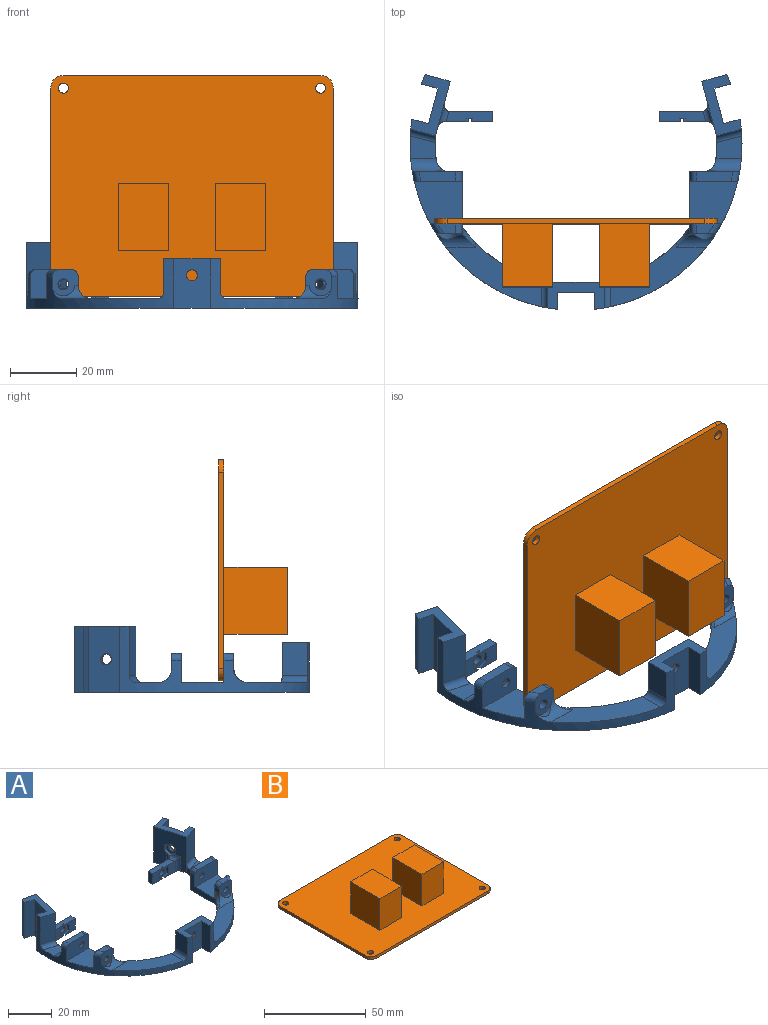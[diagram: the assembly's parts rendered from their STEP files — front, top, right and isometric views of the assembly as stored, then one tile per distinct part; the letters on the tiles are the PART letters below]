
ASSEMBLY  parts=2 mates=1
PART A: 148 faces, bbox 100.8x70.8x20.2 mm
  f0: plane 17x15mm, normal (0,1,0), area 226.7mm2, adj f1,f2,f28,f39,f41,f95,f96,f97
  f1: plane 10x7.77mm, normal (-1,0,0), area 77.7mm2, adj f0,f3,f127,f147
  f2: plane 10x7.77mm, normal (1,0,0), area 77.7mm2, adj f0,f4,f129,f147
  f3: cylinder r=50mm len=57.25mm, axis (0,0,-1), area 383.3mm2, adj f1,f5,f10,f27,f28,f29,f30,f35
  f4: cylinder r=50mm len=57.25mm, axis (0,0,-1), area 383.3mm2, adj f2,f7,f11,f23,f24,f28,f42,f43
  f5: plane 15x5.2mm, normal (1,0,0), area 77.9mm2, adj f3,f6,f28,f147
  f6: plane 15x11mm, normal (0,-1,0), area 156.4mm2, adj f5,f7,f22,f28,f147
  f7: plane 15x5.2mm, normal (-1,0,0), area 77.9mm2, adj f4,f6,f28,f147
  f8: cylinder r=1.65mm len=3.3mm, axis (0,1,0), area 31.1mm2, adj f43,f58
  f9: cylinder r=1.65mm len=3.3mm, axis (0,1,0), area 31.1mm2, adj f38,f60
  f10: cylinder r=4mm len=11.73mm, axis (1,0,0), area 33mm2, adj f3,f40,f60,f77,f146
  f11: cylinder r=4mm len=11.73mm, axis (1,0,0), area 33mm2, adj f4,f42,f43,f78,f145
  f12: plane 6.48x6mm, normal (0,-1,0), area 28mm2, adj f13,f28,f116,f132,f133,f134
  f13: plane 14.07x3.07mm, normal (0,0,1), area 40mm2, adj f12,f116,f117,f118,f124,f125,f134,f135
  f14: plane 7.09x6.07mm, normal (0,-1,0), area 31.7mm2, adj f16,f28,f122,f123,f138,f139,f140
  f15: plane 6.48x6mm, normal (0,-1,0), area 28mm2, adj f16,f28,f120,f141,f142,f143
  f16: plane 14.07x3.07mm, normal (0,0,1), area 40mm2, adj f14,f15,f119,f120,f121,f122,f140,f141
  f17: cylinder r=1.65mm len=3.3mm, axis (0,-1,0), area 20.7mm2, adj f119,f144
  f18: cylinder r=1.65mm len=3.3mm, axis (0,-1,0), area 20.7mm2, adj f117,f137
  f19: plane 20x16.42mm, normal (0.97,-0.26,0), area 256.5mm2, adj f26,f28,f29,f31,f35,f102,f103,f104
  f20: cylinder r=1.65mm len=3.58mm, axis (-0.97,-0.26,0), area 15.6mm2, adj f55,f115
  f21: cylinder r=1.65mm len=3.58mm, axis (0.97,-0.26,0), area 15.6mm2, adj f34,f108
  f22: cylinder r=1.65mm len=3.3mm, axis (0,1,0), area 15.6mm2, adj f6,f101
  f23: plane 15.18x11.9mm, normal (0,1,0), area 76.2mm2, adj f4,f24,f25,f28,f44,f57,f73,f74
  f24: cylinder r=4mm len=9.58mm, axis (-1,0,0), area 51.2mm2, adj f4,f23,f25,f47,f48,f88,f93
  f25: cylinder r=4mm len=4.88mm, axis (0,0,-1), area 23.2mm2, adj f23,f24,f28,f47,f88,f89
  f26: cylinder r=42.36mm len=7.17mm, axis (0,0,-1), area 22.4mm2, adj f19,f27,f28,f79,f80,f130
  f27: plane 7.85x6.71mm, normal (0,0,1), area 43.6mm2, adj f3,f26,f79,f130
  f28: plane 100x70.66mm, normal (0,0,-1), area 1521.3mm2, adj f0,f3,f4,f5,f6,f7,f12,f14
  f29: plane 15x7.51mm, normal (-0.26,-0.97,0), area 116.6mm2, adj f3,f19,f35,f130
  f30: plane 20x5.02mm, normal (0.26,0.97,0), area 103.9mm2, adj f3,f28,f34,f35
  f31: plane 20x7.51mm, normal (0.26,0.97,0), area 155.4mm2, adj f19,f28,f32,f35
  f32: cylinder r=50mm len=20mm, axis (0,0,-1), area 60.6mm2, adj f28,f31,f33,f35
  f33: plane 20x5.02mm, normal (-0.26,-0.97,0), area 103.9mm2, adj f28,f32,f34,f35
  f34: plane 20x10.63mm, normal (-0.97,0.26,0), area 211.4mm2, adj f21,f28,f30,f33,f35
  f35: plane 18.43x11.91mm, normal (0,0,1), area 81mm2, adj f3,f19,f29,f30,f31,f32,f33,f34
  f36: plane 18.8x9.76mm, normal (1,0,0), area 77.4mm2, adj f28,f37,f38,f60,f62,f63,f68,f69
  f37: plane 14.44x12.8mm, normal (0,0,1), area 158mm2, adj f3,f36,f38,f62
  f38: plane 9.57x8.76mm, normal (0,1,0), area 73.4mm2, adj f3,f9,f36,f37,f61,f67,f68
  f39: cylinder r=42.36mm len=25.39mm, axis (0,0,-1), area 96.7mm2, adj f0,f28,f40,f75,f77,f127
  f40: plane 28.73x19.27mm, normal (0,0,1), area 214.2mm2, adj f3,f10,f39,f77,f127
  f41: cylinder r=42.36mm len=25.39mm, axis (0,0,-1), area 96.7mm2, adj f0,f28,f42,f76,f78,f129
  f42: plane 28.73x19.27mm, normal (0,0,1), area 214.2mm2, adj f4,f11,f41,f78,f129
  f43: plane 7.95x7.79mm, normal (0,-1,0), area 43.6mm2, adj f4,f8,f11,f44,f59,f71,f72,f145
  f44: plane 18.8x9.76mm, normal (-1,0,0), area 77.4mm2, adj f23,f28,f43,f45,f46,f58,f71,f73
  f45: plane 14.44x12.8mm, normal (0,0,1), area 158mm2, adj f4,f44,f46,f58
  f46: plane 14.44x8.76mm, normal (0,-1,0), area 116.1mm2, adj f4,f44,f45,f57,f66,f73,f74
  f47: cylinder r=42.36mm len=7.17mm, axis (0,0,-1), area 22.4mm2, adj f24,f25,f28,f48,f53,f128
  f48: plane 7.85x6.71mm, normal (0,0,1), area 43.6mm2, adj f4,f24,f47,f128
  f49: plane 15x7.51mm, normal (0.26,-0.97,0), area 116.6mm2, adj f4,f53,f56,f128
  f50: plane 20x5.02mm, normal (0.26,-0.97,0), area 103.9mm2, adj f28,f51,f55,f56
  f51: cylinder r=50mm len=20mm, axis (0,0,-1), area 60.6mm2, adj f28,f50,f52,f56
  f52: plane 20x7.51mm, normal (-0.26,0.97,0), area 155.4mm2, adj f28,f51,f53,f56
  f53: plane 20x16.42mm, normal (-0.97,-0.26,0), area 256.5mm2, adj f28,f47,f49,f52,f56,f109,f110,f111
  f54: plane 20x5.02mm, normal (-0.26,0.97,0), area 103.9mm2, adj f4,f28,f55,f56
  f55: plane 20x10.63mm, normal (0.97,0.26,0), area 211.4mm2, adj f20,f28,f50,f54,f56
  f56: plane 18.43x11.91mm, normal (0,0,1), area 81mm2, adj f4,f49,f50,f51,f52,f53,f54,f55
  f57: plane 11x3mm, normal (0,0,1), area 32.1mm2, adj f23,f46,f73,f74
  f58: plane 9.57x8.76mm, normal (0,1,0), area 73.4mm2, adj f4,f8,f44,f45,f59,f71,f72
  f59: plane 5.28x3mm, normal (0,0,1), area 13.1mm2, adj f43,f58,f71,f72
  f60: plane 7.95x7.79mm, normal (0,-1,0), area 43.6mm2, adj f3,f9,f10,f36,f61,f67,f68,f146
  f61: plane 5.28x3mm, normal (0,0,1), area 13.1mm2, adj f38,f60,f67,f68
  f62: plane 14.44x8.76mm, normal (0,-1,0), area 116.1mm2, adj f3,f36,f37,f64,f65,f69,f70
  f63: plane 15.18x11.9mm, normal (0,1,0), area 76.2mm2, adj f3,f28,f36,f64,f69,f70,f79,f80
  f64: plane 11x3mm, normal (0,0,1), area 32.1mm2, adj f62,f63,f69,f70
  f65: cylinder r=1.65mm len=3.3mm, axis (0,1,0), area 15.6mm2, adj f62,f87
  f66: cylinder r=1.65mm len=3.3mm, axis (0,1,0), area 15.6mm2, adj f46,f94
  f67: torus R=48mm, axis (0,0,1), area 11mm2, adj f3,f38,f60,f61
  f68: cylinder r=2mm len=3mm, axis (0,-1,0), area 9.4mm2, adj f36,f38,f60,f61
  f69: cylinder r=2mm len=3mm, axis (0,-1,0), area 9.4mm2, adj f36,f62,f63,f64
  f70: torus R=48mm, axis (0,0,1), area 9.5mm2, adj f3,f62,f63,f64
  f71: cylinder r=2mm len=3mm, axis (0,1,0), area 9.4mm2, adj f43,f44,f58,f59
  f72: torus R=48mm, axis (0,0,1), area 11mm2, adj f4,f43,f58,f59
  f73: cylinder r=2mm len=3mm, axis (0,1,0), area 9.4mm2, adj f23,f44,f46,f57
  f74: torus R=48mm, axis (0,0,1), area 9.5mm2, adj f4,f23,f46,f57
  f75: cylinder r=2mm len=7mm, axis (0,0,-1), area 7.9mm2, adj f28,f36,f39,f77
  f76: cylinder r=2mm len=7mm, axis (0,0,-1), area 7.9mm2, adj f28,f41,f44,f78
  f77: cylinder r=4mm len=6.78mm, axis (0,1,0), area 11.5mm2, adj f10,f36,f39,f40,f75
  f78: cylinder r=4mm len=6.78mm, axis (0,-1,0), area 11.5mm2, adj f11,f41,f42,f44,f76
  f79: cylinder r=4mm len=9.58mm, axis (-1,0,0), area 51.2mm2, adj f3,f26,f27,f63,f80,f84,f86
  f80: cylinder r=4mm len=4.88mm, axis (0,0,-1), area 23.2mm2, adj f26,f28,f63,f79,f85,f86
  f81: plane 2.86x1.65mm, normal (-0.5,0,-0.87), area 5mm2, adj f63,f82,f83,f87
  f82: plane 3.3x1.5mm, normal (-1,0,0), area 5mm2, adj f63,f81,f85,f87
  f83: plane 2.86x1.65mm, normal (0.5,0,-0.87), area 5mm2, adj f63,f81,f84,f87
  f84: plane 3.3x1.73mm, normal (1,0,0), area 5.1mm2, adj f63,f79,f83,f86,f87
  f85: plane 2.86x1.65mm, normal (-0.5,0,0.87), area 5mm2, adj f63,f80,f82,f86,f87
  f86: plane 2.89x2.14mm, normal (0.5,0,0.87), area 6mm2, adj f79,f80,f84,f85,f87
  f87: plane 6.6x5.72mm, normal (0,1,0), area 19.7mm2, adj f65,f81,f82,f83,f84,f85,f86
  f88: plane 2.89x2.14mm, normal (-0.5,0,0.87), area 6mm2, adj f24,f25,f89,f93,f94
  f89: plane 2.86x1.65mm, normal (0.5,0,0.87), area 5mm2, adj f23,f25,f88,f90,f94
  f90: plane 3.3x1.5mm, normal (1,0,0), area 5mm2, adj f23,f89,f91,f94
  f91: plane 2.86x1.65mm, normal (0.5,0,-0.87), area 5mm2, adj f23,f90,f92,f94
  f92: plane 2.86x1.65mm, normal (-0.5,0,-0.87), area 5mm2, adj f23,f91,f93,f94
  f93: plane 3.3x1.73mm, normal (-1,0,0), area 5.1mm2, adj f23,f24,f88,f92,f94
  f94: plane 6.6x5.72mm, normal (0,1,0), area 19.7mm2, adj f66,f88,f89,f90,f91,f92,f93
  f95: plane 2.86x1.65mm, normal (0.5,0,-0.87), area 5mm2, adj f0,f96,f100,f101
  f96: plane 2.86x1.65mm, normal (-0.5,0,-0.87), area 5mm2, adj f0,f95,f97,f101
  f97: plane 3.3x1.5mm, normal (-1,0,0), area 5mm2, adj f0,f96,f98,f101
  f98: plane 2.86x1.65mm, normal (-0.5,0,0.87), area 5mm2, adj f0,f97,f99,f101
  f99: plane 2.86x1.65mm, normal (0.5,0,0.87), area 5mm2, adj f0,f98,f100,f101
  f100: plane 3.3x1.5mm, normal (1,0,0), area 5mm2, adj f0,f95,f99,f101
  f101: plane 6.6x5.72mm, normal (0,1,0), area 19.7mm2, adj f22,f95,f96,f97,f98,f99,f100
  f102: plane 3.3x2.8mm, normal (0.13,0.48,0.87), area 5.3mm2, adj f19,f103,f107,f108,f125
  f103: plane 3.31x2.22mm, normal (-0.13,-0.48,0.87), area 5.3mm2, adj f19,f102,f104,f108,f124,f125
  f104: plane 3.3x1.45mm, normal (-0.26,-0.97,0), area 5mm2, adj f19,f103,f105,f108
  f105: plane 3.15x2.19mm, normal (-0.13,-0.48,-0.87), area 5mm2, adj f19,f104,f106,f108
  f106: plane 3.15x2.19mm, normal (0.13,0.48,-0.87), area 5mm2, adj f19,f105,f107,f108
  f107: plane 3.3x1.45mm, normal (0.26,0.97,0), area 4.9mm2, adj f19,f102,f106,f108
  f108: plane 6.6x5.52mm, normal (0.97,-0.26,0), area 19.7mm2, adj f21,f102,f103,f104,f105,f106,f107
  f109: plane 3.3x2.8mm, normal (-0.13,0.48,0.87), area 5.3mm2, adj f53,f110,f114,f115,f122
  f110: plane 3.3x1.45mm, normal (-0.26,0.97,0), area 4.9mm2, adj f53,f109,f111,f115
  f111: plane 3.15x2.19mm, normal (-0.13,0.48,-0.87), area 4.9mm2, adj f53,f110,f112,f115
  f112: plane 3.15x2.19mm, normal (0.13,-0.48,-0.87), area 5mm2, adj f53,f111,f113,f115
  f113: plane 3.3x1.45mm, normal (0.26,-0.97,0), area 5mm2, adj f53,f112,f114,f115
  f114: plane 3.31x2.22mm, normal (0.13,-0.48,0.87), area 5.3mm2, adj f53,f109,f113,f115,f121,f122
  f115: plane 6.6x5.52mm, normal (-0.97,-0.26,0), area 19.7mm2, adj f20,f109,f110,f111,f112,f113,f114
  f116: plane 6x3mm, normal (1,0,0), area 18mm2, adj f12,f13,f28,f117
  f117: plane 12.73x6mm, normal (0,1,0), area 67.8mm2, adj f13,f18,f28,f116,f124
  f118: plane 7.09x6.07mm, normal (0,-1,0), area 31.7mm2, adj f13,f28,f125,f126,f131,f135,f136
  f119: plane 12.73x6mm, normal (0,1,0), area 67.8mm2, adj f16,f17,f28,f120,f121
  f120: plane 6x3mm, normal (-1,0,0), area 18mm2, adj f15,f16,f28,f119
  f121: cylinder r=2mm len=7.64mm, axis (0,0,-1), area 24.1mm2, adj f16,f28,f53,f114,f119,f122
  f122: cylinder r=2mm len=6.7mm, axis (0.26,-0.97,0), area 11.9mm2, adj f14,f16,f53,f109,f114,f121,f123
  f123: cylinder r=2mm len=8mm, axis (0,0,-1), area 18mm2, adj f14,f28,f53,f122
  f124: cylinder r=2mm len=7.64mm, axis (0,0,1), area 24.1mm2, adj f13,f19,f28,f103,f117,f125
  f125: cylinder r=2mm len=6.7mm, axis (0.26,0.97,0), area 11.9mm2, adj f13,f19,f102,f103,f118,f124,f126
  f126: cylinder r=2mm len=8mm, axis (0,0,1), area 18mm2, adj f19,f28,f118,f125
  f127: cylinder r=2mm len=8.23mm, axis (0,-1,0), area 24.3mm2, adj f1,f3,f39,f40
  f128: cylinder r=2mm len=8.47mm, axis (0.97,0.26,0), area 24.3mm2, adj f4,f47,f48,f49
  f129: cylinder r=2mm len=8.23mm, axis (0,1,0), area 24.3mm2, adj f2,f4,f41,f42
  f130: cylinder r=2mm len=8.47mm, axis (0.97,-0.26,0), area 24.3mm2, adj f3,f26,f27,f29
  f131: plane 2.34x1.35mm, normal (0.5,0,0.87), area 2.7mm2, adj f28,f118,f136,f137
  f132: plane 2.34x1.35mm, normal (-0.5,0,0.87), area 2.7mm2, adj f12,f28,f133,f137
  f133: plane 3.3x1mm, normal (-1,0,0), area 3.3mm2, adj f12,f132,f134,f137
  f134: plane 2.34x1.35mm, normal (-0.5,0,-0.87), area 2.7mm2, adj f12,f13,f133,f137
  f135: plane 2.34x1.35mm, normal (0.5,0,-0.87), area 2.7mm2, adj f13,f118,f136,f137
  f136: plane 3.3x1mm, normal (1,0,0), area 3.3mm2, adj f118,f131,f135,f137
  f137: plane 6x5.72mm, normal (0,-1,0), area 19.4mm2, adj f13,f18,f28,f131,f132,f133,f134,f135
  f138: plane 2.34x1.35mm, normal (-0.5,0,0.87), area 2.7mm2, adj f14,f28,f139,f144
  f139: plane 3.3x1mm, normal (-1,0,0), area 3.3mm2, adj f14,f138,f140,f144
  f140: plane 2.34x1.35mm, normal (-0.5,0,-0.87), area 2.7mm2, adj f14,f16,f139,f144
  f141: plane 2.34x1.35mm, normal (0.5,0,-0.87), area 2.7mm2, adj f15,f16,f142,f144
  f142: plane 3.3x1mm, normal (1,0,0), area 3.3mm2, adj f15,f141,f143,f144
  f143: plane 2.34x1.35mm, normal (0.5,0,0.87), area 2.7mm2, adj f15,f28,f142,f144
  f144: plane 6x5.72mm, normal (0,-1,0), area 19.4mm2, adj f16,f17,f28,f138,f139,f140,f141,f142
  f145: cylinder r=3.5mm len=6.83mm, axis (0,1,0), area 7.8mm2, adj f4,f11,f43
  f146: cylinder r=3.5mm len=6.83mm, axis (0,1,0), area 7.8mm2, adj f3,f10,f60
  f147: plane 17x8.2mm, normal (0,0,1), area 81mm2, adj f0,f1,f2,f3,f4,f5,f6,f7
PART B: 24 faces, bbox 85.1x66.7x20.6 mm
  f0: plane 85.09x66.68mm, normal (0,0,1), area 5013.3mm2, adj f1,f2,f3,f4,f5,f6,f7,f8
  f1: plane 59.06x1.6mm, normal (1,0,0), area 94.5mm2, adj f0,f2,f12,f13
  f2: cylinder r=3.81mm len=3.81mm, axis (0,0,-1), area 9.6mm2, adj f0,f1,f3,f13
  f3: plane 77.47x1.6mm, normal (0,1,0), area 124mm2, adj f0,f2,f4,f13
  f4: cylinder r=3.81mm len=3.81mm, axis (0,0,-1), area 9.6mm2, adj f0,f3,f5,f13
  f5: plane 59.06x1.6mm, normal (-1,0,0), area 94.5mm2, adj f0,f4,f6,f13
  f6: cylinder r=3.81mm len=3.81mm, axis (0,0,-1), area 9.6mm2, adj f0,f5,f7,f13
  f7: plane 77.47x1.6mm, normal (0,-1,0), area 124mm2, adj f0,f6,f12,f13
  f8: cylinder r=1.5mm len=3mm, axis (0,0,-1), area 15.1mm2, adj f0,f13
  f9: cylinder r=1.5mm len=3mm, axis (0,0,-1), area 15.1mm2, adj f0,f13
  f10: cylinder r=1.5mm len=3mm, axis (0,0,-1), area 15.1mm2, adj f0,f13
  f11: cylinder r=1.5mm len=3mm, axis (0,0,-1), area 15.1mm2, adj f0,f13
  f12: cylinder r=3.81mm len=3.81mm, axis (0,0,-1), area 9.6mm2, adj f0,f1,f7,f13
  f13: plane 85.09x66.68mm, normal (0,0,-1), area 5632.6mm2, adj f1,f2,f3,f4,f5,f6,f7,f8
  f14: plane 20.32x19mm, normal (-1,0,0), area 386.1mm2, adj f0,f15,f17,f18
  f15: plane 19x15.24mm, normal (0,-1,0), area 289.6mm2, adj f0,f14,f16,f18
  f16: plane 20.32x19mm, normal (1,0,0), area 386.1mm2, adj f0,f15,f17,f18
  f17: plane 19x15.24mm, normal (0,1,0), area 289.6mm2, adj f0,f14,f16,f18
  f18: plane 20.32x15.24mm, normal (0,0,1), area 309.7mm2, adj f14,f15,f16,f17
  f19: plane 20.32x19mm, normal (1,0,0), area 386.1mm2, adj f0,f20,f22,f23
  f20: plane 19x15.24mm, normal (0,1,0), area 289.6mm2, adj f0,f19,f21,f23
  f21: plane 20.32x19mm, normal (-1,0,0), area 386.1mm2, adj f0,f20,f22,f23
  f22: plane 19x15.24mm, normal (0,-1,0), area 289.6mm2, adj f0,f19,f21,f23
  f23: plane 20.32x15.24mm, normal (0,0,1), area 309.7mm2, adj f19,f20,f21,f22
PLACE A t=(-726.56,-294.32,-19.68)mm
PLACE B rot(axis=(1,0,0),90deg) t=(-19.11,-16.72,-16.18)mm
MATE fastened B.f10 <-> A.f8  axis (0,-1,0) through (62.17,-18.32,-12.37)mm
